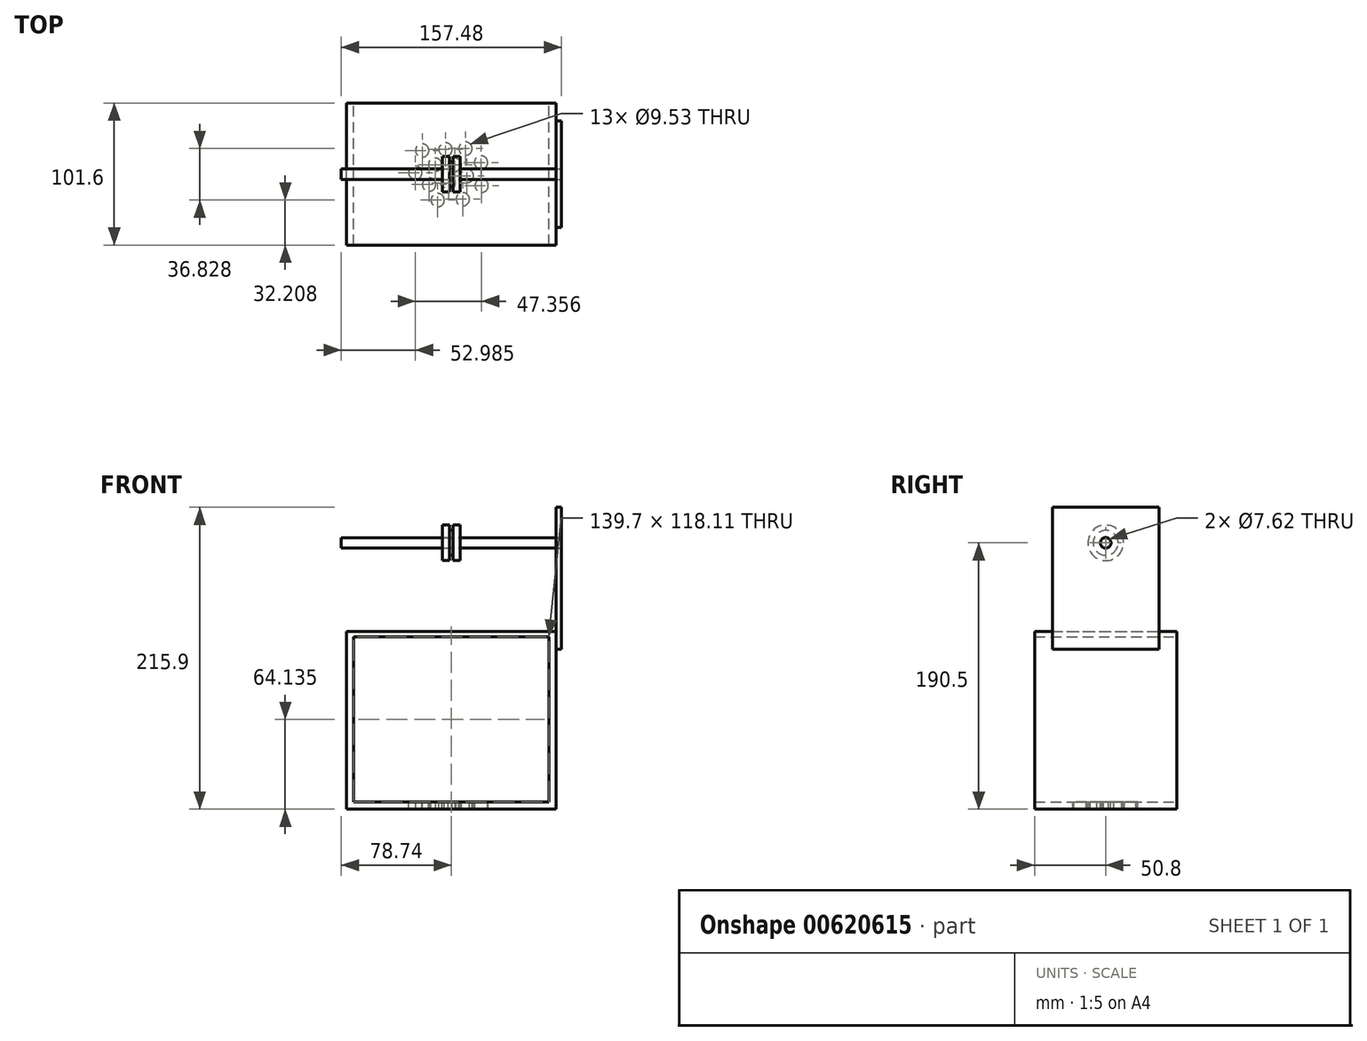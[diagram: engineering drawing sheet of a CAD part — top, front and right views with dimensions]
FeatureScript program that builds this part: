
annotation { "Feature Type Name" : "Feature", "Feature Type Description" : "" }
export const myFeature = defineFeature(function(context is Context, id is Id, definition is map)
    precondition{}
    {
        {
            var Q0;
            Q0=qCreatedBy(makeId("Front.planeOp"),FACE);
            var sketch = newSketch(context, id + "F0", { "sketchPlane" : qUnion([Q0])});
            skLineSegment(sketch, "E0", {"start": v(0, 0) * mm, "end": v(-139.7, 0) * mm});
            skLineSegment(sketch, "E1", {"start": v(-139.7, 0) * mm, "end": v(-139.7, -127) * mm});
            skLineSegment(sketch, "E2", {"start": v(-139.7, -127) * mm, "end": v(0, -127) * mm});
            skLineSegment(sketch, "E3", {"start": v(0, -127) * mm, "end": v(0, 0) * mm});
            skLineSegment(sketch, "E4", {"start": v(-139.7, -3.81) * mm, "end": v(0, -3.81) * mm});
            skLineSegment(sketch, "E5", {"start": v(0, -127) * mm, "end": v(0, -121.92) * mm});
            skLineSegment(sketch, "E6", {"start": v(0, -121.92) * mm, "end": v(-139.7, -121.92) * mm});
            skLineSegment(sketch, "E7", {"start": v(0, -121.92) * mm, "end": v(0, -118.11) * mm});
            skLineSegment(sketch, "E8", {"start": v(0, -118.11) * mm, "end": v(-139.7, -118.11) * mm});
            skLineSegment(sketch, "E9", {"start": v(-139.7, 0) * mm, "end": v(-144.78, 0) * mm});
            skLineSegment(sketch, "E10", {"start": v(-144.78, 0) * mm, "end": v(-144.78, -127) * mm});
            skLineSegment(sketch, "E11", {"start": v(-144.78, -127) * mm, "end": v(-139.7, -127) * mm});
            skLineSegment(sketch, "E12", {"start": v(0, 0) * mm, "end": v(5.08, 0) * mm});
            skLineSegment(sketch, "E13", {"start": v(5.08, 0) * mm, "end": v(5.08, -127) * mm});
            skLineSegment(sketch, "E14", {"start": v(5.08, -127) * mm, "end": v(0, -127) * mm});
            skSolve(sketch);
        }
        {
            var Q0;
            Q0 = qSketchRegion(id + "F0", true);
            extrude(context, id + "F1", {"entities" : qUnion([Q0]), "depth" : 101.6 * mm, "offsetDistance" : 25.4 * mm});
        }
        {
            var Q0;
            Q0=makeQuery(id+"F1.opExtrude","SWEPT_FACE",FACE,{"disambiguationData":[OSD([sQuery(id+"F0.wireOp",EDGE,"E13")])]});
            var sketch = newSketch(context, id + "F2", { "sketchPlane" : qUnion([Q0])});
            skLineSegment(sketch, "E15", {"start": v(-101.6, 0) * mm, "end": v(-88.9, 0) * mm});
            skLineSegment(sketch, "E16", {"start": v(0, 0) * mm, "end": v(-12.7, 0) * mm});
            skLineSegment(sketch, "E17.top", {"start": v(-88.9, -12.7) * mm, "end": v(-12.7, -12.7) * mm});
            skLineSegment(sketch, "E17.left", {"start": v(-88.9, 0) * mm, "end": v(-88.9, -12.7) * mm});
            skLineSegment(sketch, "E17.right", {"start": v(-12.7, 0) * mm, "end": v(-12.7, -12.7) * mm});
            skLineSegment(sketch, "E18", {"start": v(-88.9, 0) * mm, "end": v(-88.9, 88.9) * mm});
            skLineSegment(sketch, "E19", {"start": v(-88.9, 88.9) * mm, "end": v(-12.7, 88.9) * mm});
            skLineSegment(sketch, "E20", {"start": v(-12.7, 88.9) * mm, "end": v(-12.7, 0) * mm});
            skSolve(sketch);
        }
        {
            var Q0;
            Q0 = qSketchRegion(id + "F2", true);
            extrude(context, id + "F3", {"entities" : qUnion([Q0]), "operationType" : NewBodyOperationType.ADD, "depth" : 3.8 * mm, "offsetDistance" : 25.4 * mm});
        }
        {
            var Q0;
            Q0=makeQuery(id+"F1.opExtrude","CAP_FACE",FACE,{"disambiguationData":[OSD([sQuery(id+"F0.wireOp",EDGE,"E0"),sQuery(id+"F0.wireOp",EDGE,"E1"),sQuery(id+"F0.wireOp",EDGE,"E2"),sQuery(id+"F0.wireOp",EDGE,"E3"),sQuery(id+"F0.wireOp",EDGE,"E4"),sQuery(id+"F0.wireOp",EDGE,"E6"),sQuery(id+"F0.wireOp",EDGE,"E7"),sQuery(id+"F0.wireOp",EDGE,"E9"),sQuery(id+"F0.wireOp",EDGE,"E10"),sQuery(id+"F0.wireOp",EDGE,"E11"),sQuery(id+"F0.wireOp",EDGE,"E12"),sQuery(id+"F0.wireOp",EDGE,"E13"),sQuery(id+"F0.wireOp",EDGE,"E14")])],"isStart":false});
            var sketch = newSketch(context, id + "F4", { "sketchPlane" : qUnion([Q0])});
            skLineSegment(sketch, "E21", {"start": v(-69.85, 0) * mm, "end": v(-69.85, 66.77) * mm});
            skSolve(sketch);
        }
        {
            var Q0;
            Q0=makeQuery(id+"F1.opExtrude","CAP_EDGE",EDGE,{"disambiguationData":[OSD([sQuery(id+"F0.wireOp",EDGE,"E0"),sQuery(id+"F0.wireOp",EDGE,"E9"),sQuery(id+"F0.wireOp",EDGE,"E12")])],"isStart":true});
            cPoint(context, id + "F5", {"entities" : qUnion([Q0]), "parameter" : 0.5});
        }
        {
            var Q0;
            Q0=makeQuery(id+"F1.opExtrude","CAP_EDGE",EDGE,{"disambiguationData":[OSD([sQuery(id+"F0.wireOp",EDGE,"E6")])],"isStart":false});
            cPoint(context, id + "F6", {"entities" : qUnion([Q0]), "parameter" : 0.5});
        }
        {
            var Q0;
            Q0 = qCreatedBy(id + "F5" ,VERTEX);
            var Q1;
            Q1=sQuery(id+"F4.wireOp",VERTEX,"E21.start");
            var Q2;
            Q2 = qCreatedBy(id + "F6" ,VERTEX);
            cPlane(context, id + "F7", {"entities" : qUnion([Q0, Q1, Q2]), "cplaneType" : CPlaneType.THREE_POINT, "offset" : 25.4 * mm, "width" : 152.4 * mm, "height" : 152.4 * mm});
        }
        {
            var Q0;
            Q0=makeQuery(id+"F3.opExtrude","CAP_FACE",FACE,{"disambiguationData":[OSD([sQuery(id+"F2.wireOp",EDGE,"E17.top"),sQuery(id+"F2.wireOp",EDGE,"E17.left"),sQuery(id+"F2.wireOp",EDGE,"E17.right"),sQuery(id+"F2.wireOp",EDGE,"E18"),sQuery(id+"F2.wireOp",EDGE,"E19"),sQuery(id+"F2.wireOp",EDGE,"E20")])],"isStart":false});
            var sketch = newSketch(context, id + "F8", { "sketchPlane" : qUnion([Q0])});
            skCircle(sketch, "E22", {"center": v(-50.8, 63.5) * mm, "radius": 3.81 * mm});
            skSolve(sketch);
        }
        {
            var Q0;
            Q0 = qSketchRegion(id + "F8", true);
            extrude(context, id + "F9", {"entities" : qUnion([Q0]), "operationType" : NewBodyOperationType.REMOVE, "oppositeDirection" : true, "depth" : 25.4 * mm, "offsetDistance" : 25.4 * mm});
        }
        {
            var Q0;
            Q0=makeQuery(id+"F3.opExtrude","CAP_FACE",FACE,{"disambiguationData":[OSD([sQuery(id+"F2.wireOp",EDGE,"E17.top"),sQuery(id+"F2.wireOp",EDGE,"E17.left"),sQuery(id+"F2.wireOp",EDGE,"E17.right"),sQuery(id+"F2.wireOp",EDGE,"E18"),sQuery(id+"F2.wireOp",EDGE,"E19"),sQuery(id+"F2.wireOp",EDGE,"E20")])],"isStart":false});
            var sketch = newSketch(context, id + "F10", { "sketchPlane" : qUnion([Q0])});
            skCircle(sketch, "E23", {"center": v(-50.8, 63.5) * mm, "radius": 3.75 * mm});
            skSolve(sketch);
        }
        {
            var Q0;
            Q0 = qSketchRegion(id + "F10", true);
            extrude(context, id + "F11", {"entities" : qUnion([Q0]), "oppositeDirection" : true, "depth" : 157.48 * mm, "offsetDistance" : 25.4 * mm});
        }
        {
            var Q0;
            Q0=qCreatedBy(id+"F7.planeOp",FACE);
            var sketch = newSketch(context, id + "F12", { "sketchPlane" : qUnion([Q0])});
            skCircle(sketch, "E24.0", {"center": v(50.8, 63.5) * mm, "radius": 3.81 * mm});
            skCircle(sketch, "E25", {"center": v(50.8, 63.5) * mm, "radius": 12.7 * mm});
            skSolve(sketch);
        }
        {
            var Q0;
            Q0 = qSketchRegion(id + "F12", true);
            extrude(context, id + "F13", {"entities" : qUnion([Q0]), "endBound" : BoundingType.SYMMETRIC, "depth" : 12.7 * mm, "offsetDistance" : 25.4 * mm});
        }
        {
            var Q0;
            Q0=makeQuery(id+"F13.opExtrude","SWEPT_FACE",FACE,{"disambiguationData":[OSD([sQuery(id+"F12.wireOp",EDGE,"E25")])]});
            shell(context, id + "F14", {"entities" : qUnion([Q0]), "thickness" : 5.08 * mm});
        }
        {
            var Q0;
            Q0=makeQuery(id+"F1.opExtrude","SWEPT_FACE",FACE,{"disambiguationData":[OSD([sQuery(id+"F0.wireOp",EDGE,"E6")])]});
            var sketch = newSketch(context, id + "F15", { "sketchPlane" : qUnion([Q0])});
            skCircle(sketch, "E26", {"center": v(-90.7, -33.94) * mm, "radius": 4.76 * mm});
            skCircle(sketch, "E27", {"center": v(-95.6, -49.86) * mm, "radius": 4.76 * mm});
            skCircle(sketch, "E28", {"center": v(-81.52, -44.04) * mm, "radius": 4.76 * mm});
            skCircle(sketch, "E29", {"center": v(-74.02, -33.18) * mm, "radius": 4.76 * mm});
            skCircle(sketch, "E30", {"center": v(-67.44, -44.2) * mm, "radius": 4.76 * mm});
            skCircle(sketch, "E31", {"center": v(-71.73, -57.06) * mm, "radius": 4.76 * mm});
            skCircle(sketch, "E32", {"center": v(-85.8, -58.28) * mm, "radius": 4.76 * mm});
            skCircle(sketch, "E33", {"center": v(-59.79, -32.56) * mm, "radius": 4.76 * mm});
            skCircle(sketch, "E34", {"center": v(-58.71, -52.16) * mm, "radius": 4.76 * mm});
            skSolve(sketch);
        }
        {
            var Q0;
            Q0=makeQuery(id+"F15.imprint","IMPRINT",FACE,{"disambiguationData":[TD([[makeQuery(id+"F15.imprint","IMPRINT",EDGE,{"derivedFrom":sQuery(id+"F15.wireOp",EDGE,"E27")}),1.0]])]});
            var Q1;
            Q1=makeQuery(id+"F15.imprint","IMPRINT",FACE,{"disambiguationData":[TD([[makeQuery(id+"F15.imprint","IMPRINT",EDGE,{"derivedFrom":sQuery(id+"F15.wireOp",EDGE,"E32")}),1.0]])]});
            var Q2;
            Q2=makeQuery(id+"F15.imprint","IMPRINT",FACE,{"disambiguationData":[TD([[makeQuery(id+"F15.imprint","IMPRINT",EDGE,{"derivedFrom":sQuery(id+"F15.wireOp",EDGE,"E28")}),1.0]])]});
            var Q3;
            Q3=makeQuery(id+"F15.imprint","IMPRINT",FACE,{"disambiguationData":[TD([[makeQuery(id+"F15.imprint","IMPRINT",EDGE,{"derivedFrom":sQuery(id+"F15.wireOp",EDGE,"E26")}),1.0]])]});
            var Q4;
            Q4=makeQuery(id+"F15.imprint","IMPRINT",FACE,{"disambiguationData":[TD([[makeQuery(id+"F15.imprint","IMPRINT",EDGE,{"derivedFrom":sQuery(id+"F15.wireOp",EDGE,"E29")}),1.0]])]});
            var Q5;
            Q5=makeQuery(id+"F15.imprint","IMPRINT",FACE,{"disambiguationData":[TD([[makeQuery(id+"F15.imprint","IMPRINT",EDGE,{"derivedFrom":sQuery(id+"F15.wireOp",EDGE,"E30")}),1.0]])]});
            var Q6;
            Q6=makeQuery(id+"F15.imprint","IMPRINT",FACE,{"disambiguationData":[TD([[makeQuery(id+"F15.imprint","IMPRINT",EDGE,{"derivedFrom":sQuery(id+"F15.wireOp",EDGE,"E31")}),1.0]])]});
            var Q7;
            Q7=makeQuery(id+"F15.imprint","IMPRINT",FACE,{"disambiguationData":[TD([[makeQuery(id+"F15.imprint","IMPRINT",EDGE,{"derivedFrom":sQuery(id+"F15.wireOp",EDGE,"E34")}),1.0]])]});
            var Q8;
            Q8=makeQuery(id+"F15.imprint","IMPRINT",FACE,{"disambiguationData":[TD([[makeQuery(id+"F15.imprint","IMPRINT",EDGE,{"derivedFrom":sQuery(id+"F15.wireOp",EDGE,"E33")}),1.0]])]});
            var Q9;
            Q9=sQuery(id+"F15.wireOp",EDGE,"E26");
            var Q10;
            Q10=sQuery(id+"F15.wireOp",EDGE,"E27");
            var Q11;
            Q11=sQuery(id+"F15.wireOp",EDGE,"E32");
            var Q12;
            Q12=sQuery(id+"F15.wireOp",EDGE,"E28");
            var Q13;
            Q13=sQuery(id+"F15.wireOp",EDGE,"E31");
            var Q14;
            Q14=sQuery(id+"F15.wireOp",EDGE,"E30");
            var Q15;
            Q15=sQuery(id+"F15.wireOp",EDGE,"E33");
            extrude(context, id + "F16", {"entities" : qUnion([Q0, Q1, Q2, Q3, Q4, Q5, Q6, Q7, Q8]), "operationType" : NewBodyOperationType.REMOVE, "surfaceEntities" : qUnion([Q9, Q10, Q11, Q12, Q13, Q14, Q15]), "endBound" : BoundingType.UP_TO_NEXT, "oppositeDirection" : true, "depth" : 25.4 * mm, "offsetDistance" : 25.4 * mm});
        }
        {
            var Q0;
            Q0=makeQuery(id+"F1.opExtrude","SWEPT_FACE",FACE,{"disambiguationData":[OSD([sQuery(id+"F0.wireOp",EDGE,"E6")])]});
            var sketch = newSketch(context, id + "F17", { "sketchPlane" : qUnion([Q0])});
            skCircle(sketch, "E35", {"center": v(-48.68, -42.46) * mm, "radius": 4.76 * mm});
            skCircle(sketch, "E36", {"center": v(-61.73, -68.78) * mm, "radius": 4.76 * mm});
            skCircle(sketch, "E37", {"center": v(-79.69, -69.4) * mm, "radius": 4.76 * mm});
            skCircle(sketch, "E38", {"center": v(-48.25, -59.1) * mm, "radius": 4.76 * mm});
            skSolve(sketch);
        }
        {
            var Q0;
            Q0 = qSketchRegion(id + "F17", true);
            extrude(context, id + "F18", {"entities" : qUnion([Q0]), "operationType" : NewBodyOperationType.REMOVE, "oppositeDirection" : true, "depth" : 25.4 * mm, "offsetDistance" : 25.4 * mm});
        }
    });
